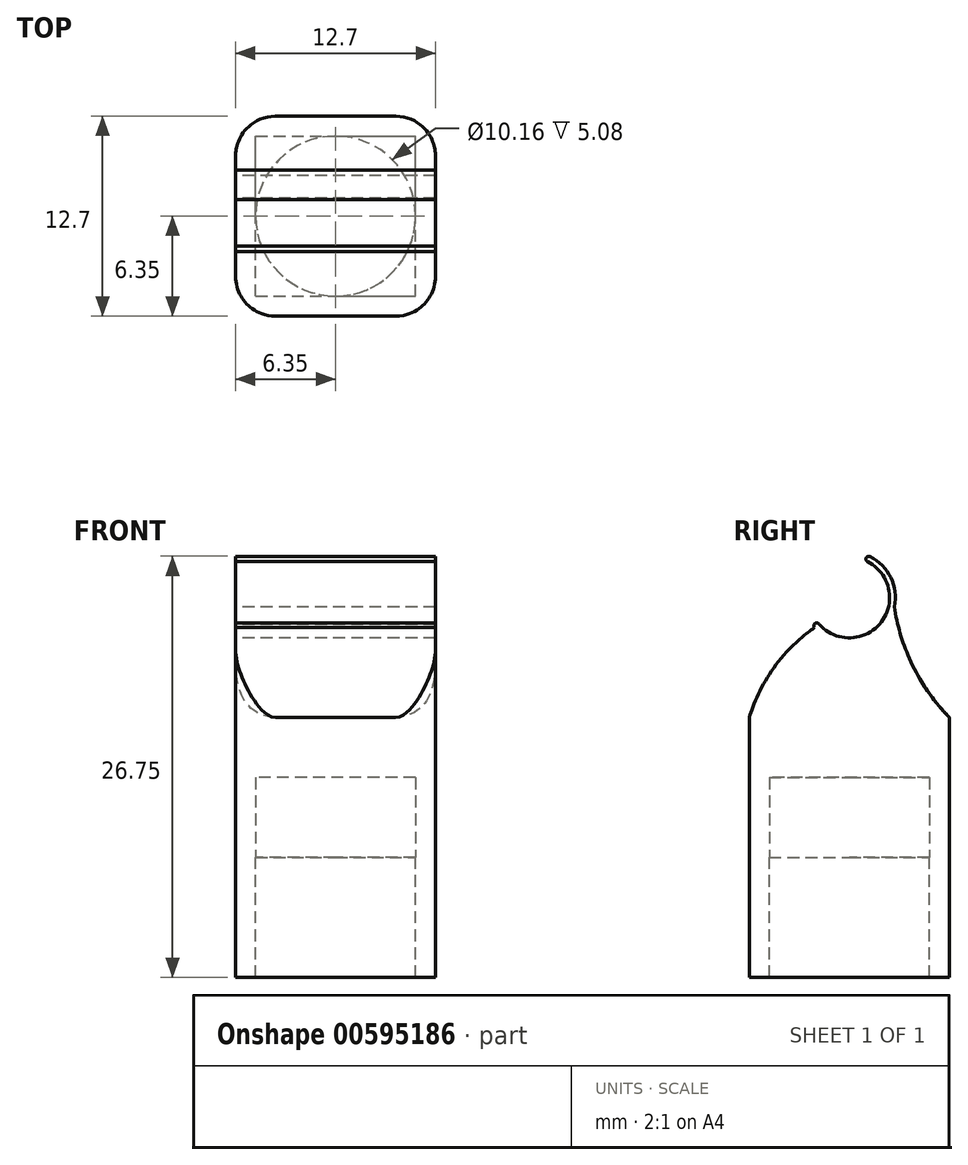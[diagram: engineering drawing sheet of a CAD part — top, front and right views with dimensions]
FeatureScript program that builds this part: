
annotation { "Feature Type Name" : "Feature", "Feature Type Description" : "" }
export const myFeature = defineFeature(function(context is Context, id is Id, definition is map)
    precondition{}
    {
        {
            var Q0;
            Q0=qCreatedBy(makeId("Top.planeOp"),FACE);
            var sketch = newSketch(context, id + "F0", { "sketchPlane" : qUnion([Q0])});
            skLineSegment(sketch, "E0.bottom", {"start": v(-3.81, 6.35) * mm, "end": v(3.81, 6.35) * mm});
            skLineSegment(sketch, "E0.top", {"start": v(-3.81, -6.35) * mm, "end": v(3.81, -6.35) * mm});
            skLineSegment(sketch, "E0.left", {"start": v(-6.35, 3.81) * mm, "end": v(-6.35, -3.81) * mm});
            skLineSegment(sketch, "E0.right", {"start": v(6.35, 3.81) * mm, "end": v(6.35, -3.8) * mm});
            skCircle(sketch, "E1", {"center": v(0, 0) * mm, "radius": 5.08 * mm});
            skPoint(sketch, "E2.visualSharp", {"position": v(-6.35, -6.35) * mm});
            skArc(sketch, "E2.filletArc", {"start": v(-6.35, -3.81) * mm, "mid": v(-5.6, -5.6) * mm, "end": v(-3.8, -6.35) * mm});
            skPoint(sketch, "E3.visualSharp", {"position": v(-6.35, 6.35) * mm});
            skArc(sketch, "E3.filletArc", {"start": v(-3.81, 6.35) * mm, "mid": v(-5.6, 5.6) * mm, "end": v(-6.35, 3.81) * mm});
            skPoint(sketch, "E4.visualSharp", {"position": v(6.35, 6.35) * mm});
            skArc(sketch, "E4.filletArc", {"start": v(6.35, 3.81) * mm, "mid": v(5.6, 5.6) * mm, "end": v(3.81, 6.35) * mm});
            skPoint(sketch, "E5.visualSharp", {"position": v(6.35, -6.35) * mm});
            skArc(sketch, "E5.filletArc", {"start": v(3.81, -6.35) * mm, "mid": v(5.6, -5.6) * mm, "end": v(6.35, -3.8) * mm});
            skSolve(sketch);
        }
        {
            var Q0;
            Q0=makeQuery(id+"F0.imprint","IMPRINT",FACE,{"disambiguationData":[TD([[makeQuery(id+"F0.imprint","IMPRINT",EDGE,{"derivedFrom":sQuery(id+"F0.wireOp",EDGE,"E0.bottom")}),-1.0]])]});
            extrude(context, id + "F1", {"entities" : qUnion([Q0]), "depth" : 5.08 * mm, "offsetDistance" : 25.4 * mm});
        }
        {
            var Q0;
            Q0=makeQuery(id+"F1.opExtrude","CAP_FACE",FACE,{"disambiguationData":[OSD([sQuery(id+"F0.wireOp",EDGE,"E0.bottom"),sQuery(id+"F0.wireOp",EDGE,"E0.top"),sQuery(id+"F0.wireOp",EDGE,"E0.left"),sQuery(id+"F0.wireOp",EDGE,"E0.right"),sQuery(id+"F0.wireOp",EDGE,"E1"),sQuery(id+"F0.wireOp",EDGE,"E2.filletArc"),sQuery(id+"F0.wireOp",EDGE,"E3.filletArc"),sQuery(id+"F0.wireOp",EDGE,"E4.filletArc"),sQuery(id+"F0.wireOp",EDGE,"E5.filletArc")])],"isStart":false});
            var sketch = newSketch(context, id + "F2", { "sketchPlane" : qUnion([Q0])});
            skLineSegment(sketch, "E6", {"start": v(-6.35, 3.81) * mm, "end": v(-6.35, -3.81) * mm});
            skLineSegment(sketch, "E7", {"start": v(-3.8, -6.35) * mm, "end": v(3.81, -6.35) * mm});
            skLineSegment(sketch, "E8", {"start": v(6.35, -3.8) * mm, "end": v(6.35, 3.81) * mm});
            skLineSegment(sketch, "E9", {"start": v(-3.81, 6.35) * mm, "end": v(3.81, 6.35) * mm});
            skArc(sketch, "E10", {"start": v(-3.81, 6.35) * mm, "mid": v(-5.6, 5.6) * mm, "end": v(-6.35, 3.81) * mm});
            skArc(sketch, "E11.MirrorCS", {"start": v(3.81, 6.35) * mm, "mid": v(5.6, 5.6) * mm, "end": v(6.35, 3.81) * mm});
            skArc(sketch, "E12.MirrorCS", {"start": v(-3.81, -6.35) * mm, "mid": v(-5.6, -5.6) * mm, "end": v(-6.35, -3.81) * mm});
            skArc(sketch, "E13.MirrorCS", {"start": v(3.81, -6.35) * mm, "mid": v(5.6, -5.6) * mm, "end": v(6.35, -3.81) * mm});
            skLineSegment(sketch, "E14.MirrorCS", {"start": v(6.35, 3.81) * mm, "end": v(6.35, -3.81) * mm});
            skSolve(sketch);
        }
        {
            var Q0;
            Q0=makeQuery(id+"F2.imprint","IMPRINT",FACE,{"disambiguationData":[TD([[makeQuery(id+"F2.imprint","IMPRINT",EDGE,{"derivedFrom":makeQuery(id+"F1.opExtrude","CAP_EDGE",EDGE,{"disambiguationData":[OSD([sQuery(id+"F0.wireOp",EDGE,"E1")])],"isStart":false})}),1.0]])]});
            var Q1;
            Q1=makeQuery(id+"F2.imprint","IMPRINT",FACE,{"disambiguationData":[TD([[makeQuery(id+"F2.imprint","IMPRINT",EDGE,{"derivedFrom":sQuery(id+"F2.wireOp",EDGE,"E7")}),1.0]])]});
            extrude(context, id + "F3", {"entities" : qUnion([Q0, Q1]), "operationType" : NewBodyOperationType.ADD, "depth" : 3.8 * mm, "offsetDistance" : 25.4 * mm});
        }
        {
            var Q0;
            Q0=makeQuery(id+"F3.boolean.opBoolean","MERGE",FACE,{"derivedFrom":[makeQuery(id+"F1.opExtrude","SWEPT_FACE",FACE,{"disambiguationData":[OSD([sQuery(id+"F0.wireOp",EDGE,"E0.left")])]}),makeQuery(id+"F3.opExtrude","SWEPT_FACE",FACE,{"disambiguationData":[OSD([sQuery(id+"F2.wireOp",EDGE,"E6")])]})]});
            var sketch = newSketch(context, id + "F4", { "sketchPlane" : qUnion([Q0])});
            skLineSegment(sketch, "E15.bottom", {"start": v(-6.35, 8.9) * mm, "end": v(6.35, 8.89) * mm});
            skArc(sketch, "E16", {"start": v(-6.35, 8.9) * mm, "mid": v(-4.05, 12.13) * mm, "end": v(-2.86, 15.91) * mm});
            skArc(sketch, "E17", {"start": v(2.21, 14.6) * mm, "mid": v(4.76, 12.1) * mm, "end": v(6.35, 8.89) * mm});
            skArc(sketch, "E18", {"start": v(-1.14, 18.8) * mm, "mid": v(-2.03, 14.95) * mm, "end": v(1.91, 14.8) * mm});
            skArc(sketch, "E19", {"start": v(-1.32, 19.1) * mm, "mid": v(-2.63, 17.77) * mm, "end": v(-2.86, 15.91) * mm});
            skArc(sketch, "E20", {"start": v(-1.17, 18.78) * mm, "mid": v(-1.07, 19.02) * mm, "end": v(-1.32, 19.1) * mm});
            skPoint(sketch, "E20.second.point", {"position": v(-1.32, 19.1) * mm});
            skPoint(sketch, "E20.third.point", {"position": v(-1.32, 19.1) * mm});
            skArc(sketch, "E21", {"start": v(2.21, 14.6) * mm, "mid": v(2.18, 14.87) * mm, "end": v(1.91, 14.8) * mm});
            skPoint(sketch, "E21.second.point", {"position": v(2.21, 14.6) * mm});
            skPoint(sketch, "E21.third.point", {"position": v(2.21, 14.6) * mm});
            skSolve(sketch);
        }
        {
            var Q0;
            {var subQ0=sQuery(id+"F4.wireOp",EDGE,"E16");Q0=makeQuery(id+"F4.imprint","IMPRINT",FACE,{"disambiguationData":[TD([[makeQuery(id+"F4.imprint","IMPRINT",EDGE,{"derivedFrom":subQ0}),-1.0]])]});}
            var Q1;
            Q1=makeQuery(id+"F3.boolean.opBoolean","MERGE",FACE,{"derivedFrom":[makeQuery(id+"F1.opExtrude","SWEPT_FACE",FACE,{"disambiguationData":[OSD([sQuery(id+"F0.wireOp",EDGE,"E0.right")])]}),makeQuery(id+"F3.opExtrude","SWEPT_FACE",FACE,{"disambiguationData":[OSD([sQuery(id+"F2.wireOp",EDGE,"E14.MirrorCS")])]})]});
            extrude(context, id + "F5", {"entities" : qUnion([Q0]), "operationType" : NewBodyOperationType.ADD, "endBound" : BoundingType.UP_TO_SURFACE, "oppositeDirection" : true, "depth" : 25.4 * mm, "endBoundEntityFace" : qUnion([Q1]), "offsetDistance" : 25.4 * mm});
        }
        {
            var Q0;
            Q0=makeQuery(id+"F1.opExtrude","CAP_FACE",FACE,{"disambiguationData":[OSD([sQuery(id+"F0.wireOp",EDGE,"E0.bottom"),sQuery(id+"F0.wireOp",EDGE,"E0.top"),sQuery(id+"F0.wireOp",EDGE,"E0.left"),sQuery(id+"F0.wireOp",EDGE,"E0.right"),sQuery(id+"F0.wireOp",EDGE,"E1"),sQuery(id+"F0.wireOp",EDGE,"E2.filletArc"),sQuery(id+"F0.wireOp",EDGE,"E3.filletArc"),sQuery(id+"F0.wireOp",EDGE,"E4.filletArc"),sQuery(id+"F0.wireOp",EDGE,"E5.filletArc")])],"isStart":true});
            var sketch = newSketch(context, id + "F6", { "sketchPlane" : qUnion([Q0])});
            skLineSegment(sketch, "E22.bottom", {"start": v(7.26, -7.24) * mm, "end": v(-7.84, -7.24) * mm});
            skLineSegment(sketch, "E22.top", {"start": v(7.26, 7.08) * mm, "end": v(-7.84, 7.08) * mm});
            skLineSegment(sketch, "E22.left", {"start": v(7.26, -7.24) * mm, "end": v(7.26, 7.08) * mm});
            skLineSegment(sketch, "E22.right", {"start": v(-7.84, -7.24) * mm, "end": v(-7.84, 7.08) * mm});
            skLineSegment(sketch, "E23", {"start": v(6.35, 3.8) * mm, "end": v(6.35, -3.81) * mm});
            skLineSegment(sketch, "E24", {"start": v(3.81, -6.35) * mm, "end": v(-3.81, -6.35) * mm});
            skArc(sketch, "E25", {"start": v(3.81, -6.35) * mm, "mid": v(5.6, -5.6) * mm, "end": v(6.35, -3.81) * mm});
            skArc(sketch, "E26.MirrorCS", {"start": v(3.81, 6.35) * mm, "mid": v(5.6, 5.6) * mm, "end": v(6.35, 3.81) * mm});
            skLineSegment(sketch, "E27.MirrorCS", {"start": v(6.35, -3.8) * mm, "end": v(6.35, 3.81) * mm});
            skLineSegment(sketch, "E28.MirrorCS", {"start": v(3.81, 6.35) * mm, "end": v(-3.81, 6.35) * mm});
            skSolve(sketch);
        }
        {
            var Q0;
            Q0=makeQuery(id+"F6.imprint","IMPRINT",FACE,{"disambiguationData":[TD([[makeQuery(id+"F6.imprint","IMPRINT",EDGE,{"derivedFrom":sQuery(id+"F6.wireOp",EDGE,"E22.bottom")}),-1.0]])]});
            extrude(context, id + "F7", {"entities" : qUnion([Q0]), "operationType" : NewBodyOperationType.REMOVE, "oppositeDirection" : true, "depth" : 25.4 * mm, "offsetDistance" : 25.4 * mm});
        }
        {
            var Q0;
            Q0=makeQuery(id+"F1.opExtrude","CAP_FACE",FACE,{"disambiguationData":[OSD([sQuery(id+"F0.wireOp",EDGE,"E0.bottom"),sQuery(id+"F0.wireOp",EDGE,"E0.top"),sQuery(id+"F0.wireOp",EDGE,"E0.left"),sQuery(id+"F0.wireOp",EDGE,"E0.right"),sQuery(id+"F0.wireOp",EDGE,"E1"),sQuery(id+"F0.wireOp",EDGE,"E2.filletArc"),sQuery(id+"F0.wireOp",EDGE,"E3.filletArc"),sQuery(id+"F0.wireOp",EDGE,"E4.filletArc"),sQuery(id+"F0.wireOp",EDGE,"E5.filletArc")])],"isStart":true});
            var sketch = newSketch(context, id + "F8", { "sketchPlane" : qUnion([Q0])});
            skLineSegment(sketch, "E29.bottom", {"start": v(-5.08, 5.08) * mm, "end": v(5.08, 5.08) * mm});
            skLineSegment(sketch, "E29.top", {"start": v(-5.08, -5.08) * mm, "end": v(5.08, -5.08) * mm});
            skLineSegment(sketch, "E29.left", {"start": v(-5.08, 5.08) * mm, "end": v(-5.08, -5.08) * mm});
            skLineSegment(sketch, "E29.right", {"start": v(5.08, 5.08) * mm, "end": v(5.08, -5.08) * mm});
            skLineSegment(sketch, "E30.bottom", {"start": v(-3.8, 6.35) * mm, "end": v(3.81, 6.35) * mm});
            skLineSegment(sketch, "E30.top", {"start": v(-3.8, -6.35) * mm, "end": v(3.81, -6.35) * mm});
            skLineSegment(sketch, "E30.left", {"start": v(-6.35, 3.81) * mm, "end": v(-6.35, -3.81) * mm});
            skLineSegment(sketch, "E30.right", {"start": v(6.35, 3.81) * mm, "end": v(6.35, -3.81) * mm});
            skPoint(sketch, "E31.visualSharp", {"position": v(-6.35, 6.35) * mm});
            skArc(sketch, "E31.filletArc", {"start": v(-3.8, 6.35) * mm, "mid": v(-5.6, 5.6) * mm, "end": v(-6.35, 3.81) * mm});
            skPoint(sketch, "E32.visualSharp", {"position": v(6.35, 6.35) * mm});
            skArc(sketch, "E32.filletArc", {"start": v(6.35, 3.81) * mm, "mid": v(5.6, 5.6) * mm, "end": v(3.81, 6.35) * mm});
            skPoint(sketch, "E33.visualSharp", {"position": v(6.35, -6.35) * mm});
            skArc(sketch, "E33.filletArc", {"start": v(3.81, -6.35) * mm, "mid": v(5.6, -5.6) * mm, "end": v(6.35, -3.81) * mm});
            skPoint(sketch, "E34.visualSharp", {"position": v(-6.35, -6.35) * mm});
            skArc(sketch, "E34.filletArc", {"start": v(-6.35, -3.81) * mm, "mid": v(-5.6, -5.6) * mm, "end": v(-3.8, -6.35) * mm});
            skSolve(sketch);
        }
        {
            var Q0;
            Q0=makeQuery(id+"F8.imprint","IMPRINT",FACE,{"disambiguationData":[TD([[makeQuery(id+"F8.imprint","IMPRINT",EDGE,{"derivedFrom":sQuery(id+"F8.wireOp",EDGE,"E30.bottom")}),-1.0]])]});
            extrude(context, id + "F9", {"entities" : qUnion([Q0]), "operationType" : NewBodyOperationType.ADD, "depth" : 7.62 * mm, "offsetDistance" : 25.4 * mm});
        }
    });
